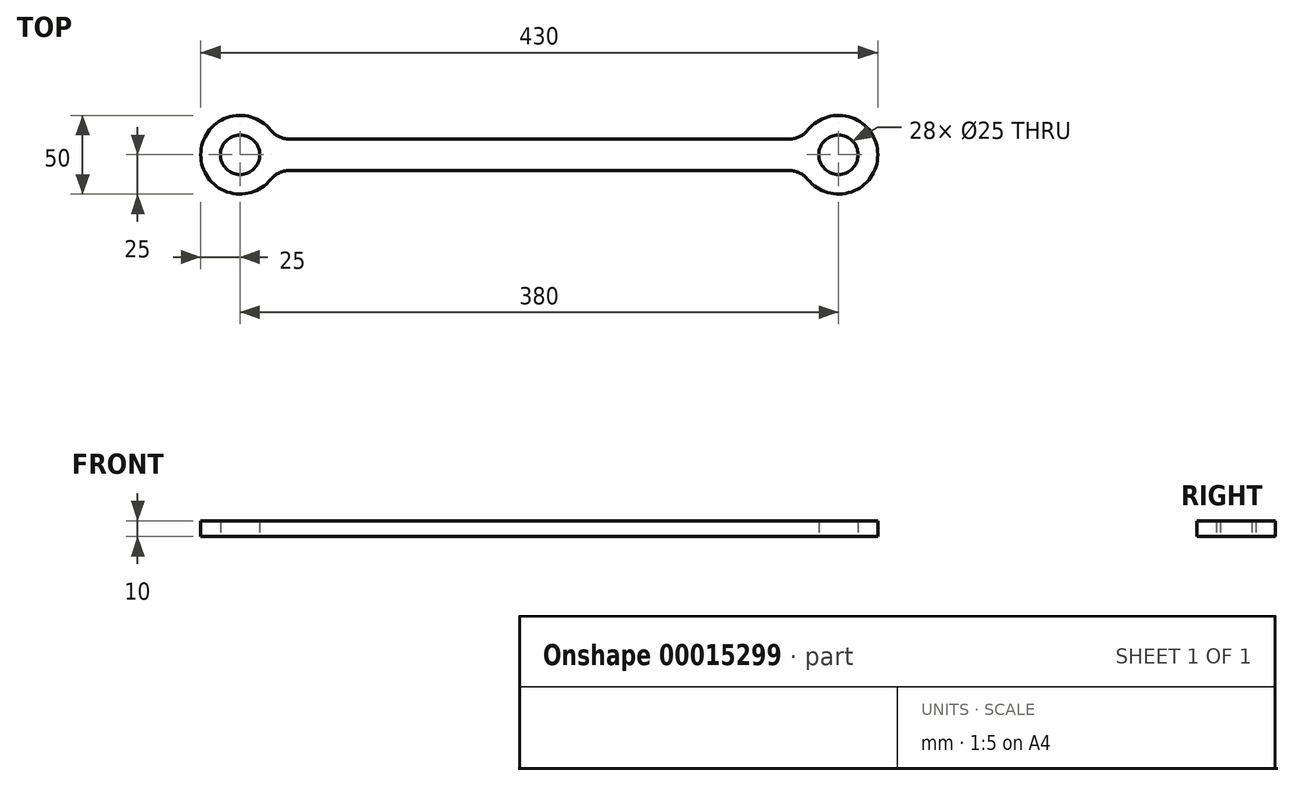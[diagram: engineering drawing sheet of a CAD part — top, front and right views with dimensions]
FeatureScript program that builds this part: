
annotation { "Feature Type Name" : "Feature", "Feature Type Description" : "" }
export const myFeature = defineFeature(function(context is Context, id is Id, definition is map)
    precondition{}
    {
        {
            var Q0;
            Q0=qCreatedBy(makeId("Top.planeOp"),FACE);
            var sketch = newSketch(context, id + "F0", { "sketchPlane" : qUnion([Q0])});
            skArc(sketch, "E0", {"start": v(19.52, 15.63) * mm, "mid": v(-25, 0) * mm, "end": v(19.52, -15.63) * mm});
            skArc(sketch, "E1", {"start": v(360.48, -15.63) * mm, "mid": v(405, 0) * mm, "end": v(360.48, 15.63) * mm});
            skLineSegment(sketch, "E2", {"start": v(31.22, 10) * mm, "end": v(348.78, 10) * mm});
            skLineSegment(sketch, "E3", {"start": v(0, 0) * mm, "end": v(380, 0) * mm, "construction": true});
            skLineSegment(sketch, "E4.MirrorCS", {"start": v(31.22, -10) * mm, "end": v(348.78, -10) * mm});
            skPoint(sketch, "E5.visualSharp", {"position": v(22.91, 10) * mm});
            skArc(sketch, "E5.filletArc", {"start": v(19.52, 15.62) * mm, "mid": v(24.73, 11.48) * mm, "end": v(31.22, 10) * mm});
            skPoint(sketch, "E6.visualSharp", {"position": v(22.91, -10) * mm});
            skArc(sketch, "E6.filletArc", {"start": v(31.22, -10) * mm, "mid": v(24.73, -11.48) * mm, "end": v(19.52, -15.62) * mm});
            skPoint(sketch, "E7.visualSharp", {"position": v(357.09, -10) * mm});
            skArc(sketch, "E7.filletArc", {"start": v(360.48, -15.63) * mm, "mid": v(355.27, -11.48) * mm, "end": v(348.78, -10) * mm});
            skPoint(sketch, "E8.visualSharp", {"position": v(357.09, 10) * mm});
            skArc(sketch, "E8.filletArc", {"start": v(348.78, 10) * mm, "mid": v(355.27, 11.48) * mm, "end": v(360.48, 15.63) * mm});
            skCircle(sketch, "E9", {"center": v(0, 0) * mm, "radius": 12.5 * mm});
            skCircle(sketch, "E10", {"center": v(380, 0) * mm, "radius": 12.5 * mm});
            skSolve(sketch);
        }
        {
            var Q0;
            Q0 = qSketchRegion(id + "F0", true);
            extrude(context, id + "F1", {"entities" : qUnion([Q0]), "depth" : 10 * mm});
        }
    });
